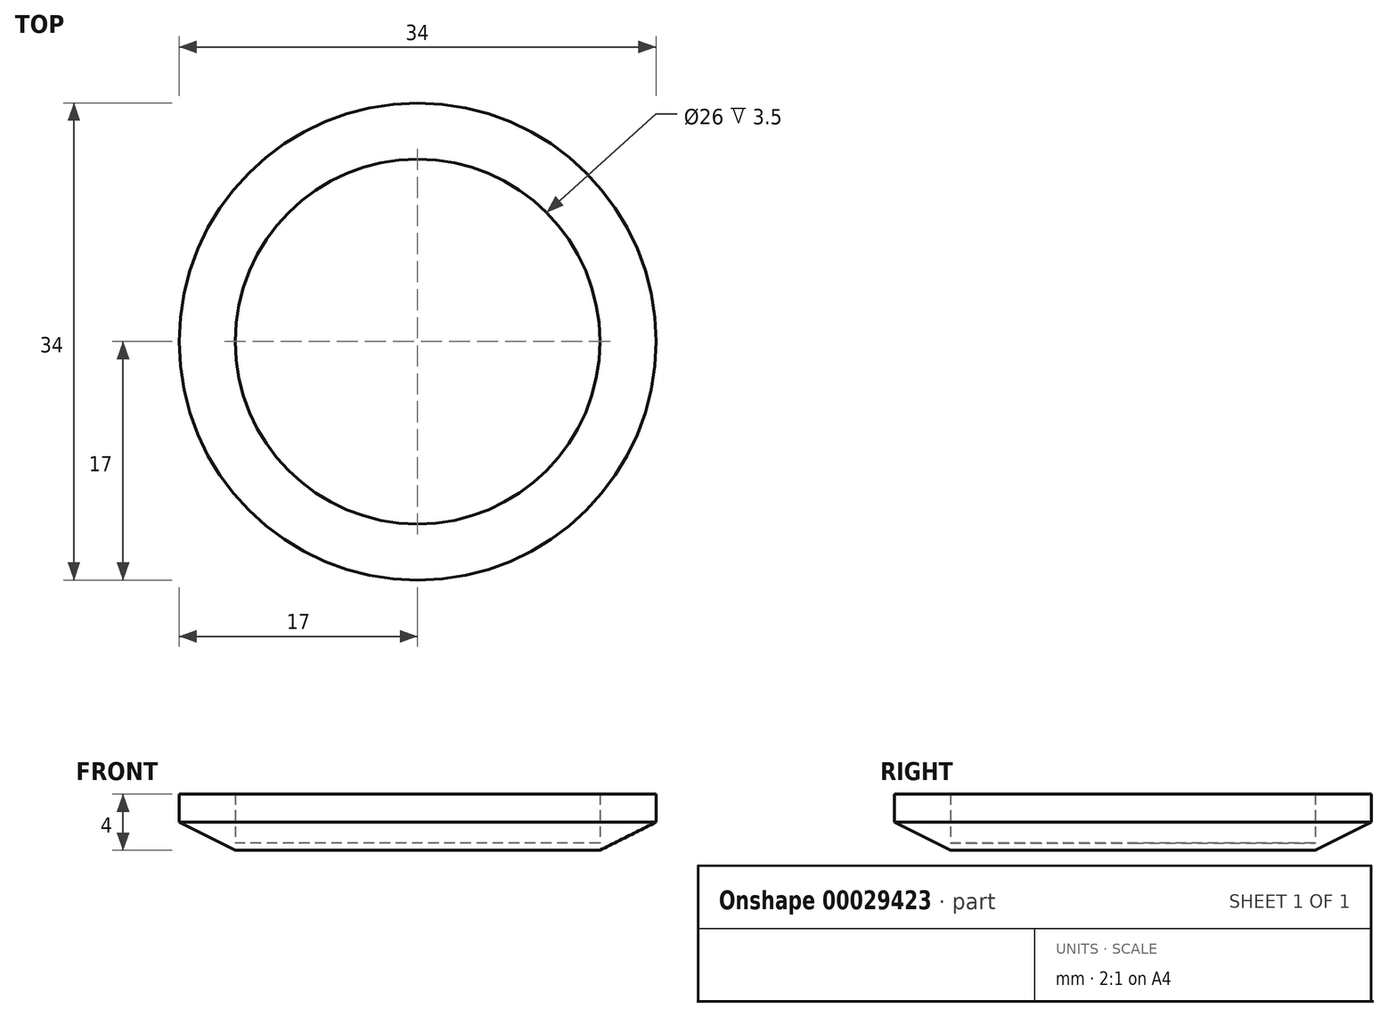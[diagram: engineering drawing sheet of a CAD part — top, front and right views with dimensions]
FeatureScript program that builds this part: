
annotation { "Feature Type Name" : "Feature", "Feature Type Description" : "" }
export const myFeature = defineFeature(function(context is Context, id is Id, definition is map)
    precondition{}
    {
        {
            assignVariable(context, id + "F0", {"name" : "MagnetThickness", "anyValue" : 3.5});
        }
        {
            assignVariable(context, id + "F1", {"name" : "Padding", "anyValue" : 4});
        }
        {
            assignVariable(context, id + "F2", {"name" : "UnderMagnetThickness", "anyValue" : 0.5});
        }
        {
            var Q0;
            Q0=qCreatedBy(makeId("Top.planeOp"),FACE);
            var sketch = newSketch(context, id + "F3", { "sketchPlane" : qUnion([Q0])});
            skCircle(sketch, "E0", {"center": v(0, 0) * mm, "radius": 13 * mm});
            skCircle(sketch, "E1", {"center": v(0, 0) * mm, "radius": 17 * mm});
            skSolve(sketch);
        }
        {
            var Q0;
            Q0=makeQuery(id+"F3.imprint","IMPRINT",FACE,{"disambiguationData":[TD([[makeQuery(id+"F3.imprint","IMPRINT",EDGE,{"derivedFrom":sQuery(id+"F3.wireOp",EDGE,"E0")}),1.0]])]});
            extrude(context, id + "F4", {"entities" : qUnion([Q0]), "depth" : (getVariable(context, 'UnderMagnetThickness')) * mm});
        }
        {
            var Q0;
            Q0=makeQuery(id+"F3.imprint","IMPRINT",FACE,{"disambiguationData":[TD([[makeQuery(id+"F3.imprint","IMPRINT",EDGE,{"derivedFrom":sQuery(id+"F3.wireOp",EDGE,"E0")}),-1.0]])]});
            extrude(context, id + "F5", {"entities" : qUnion([Q0]), "operationType" : NewBodyOperationType.ADD, "depth" : (getVariable(context, 'MagnetThickness') + getVariable(context, 'UnderMagnetThickness')) * mm});
        }
        {
            var Q0;
            Q0=makeQuery(id+"F5.opExtrude","CAP_EDGE",EDGE,{"disambiguationData":[OSD([sQuery(id+"F3.wireOp",EDGE,"E1")])],"isStart":true});
            chamfer(context, id + "F6", {"entities" : qUnion([Q0]), "chamferType" : ChamferType.TWO_OFFSETS, "width1" : (getVariable(context, 'Padding') / 2) * mm, "oppositeDirection" : false, "width2" : (getVariable(context, 'Padding')) * mm, "tangentPropagation" : true});
        }
    });
